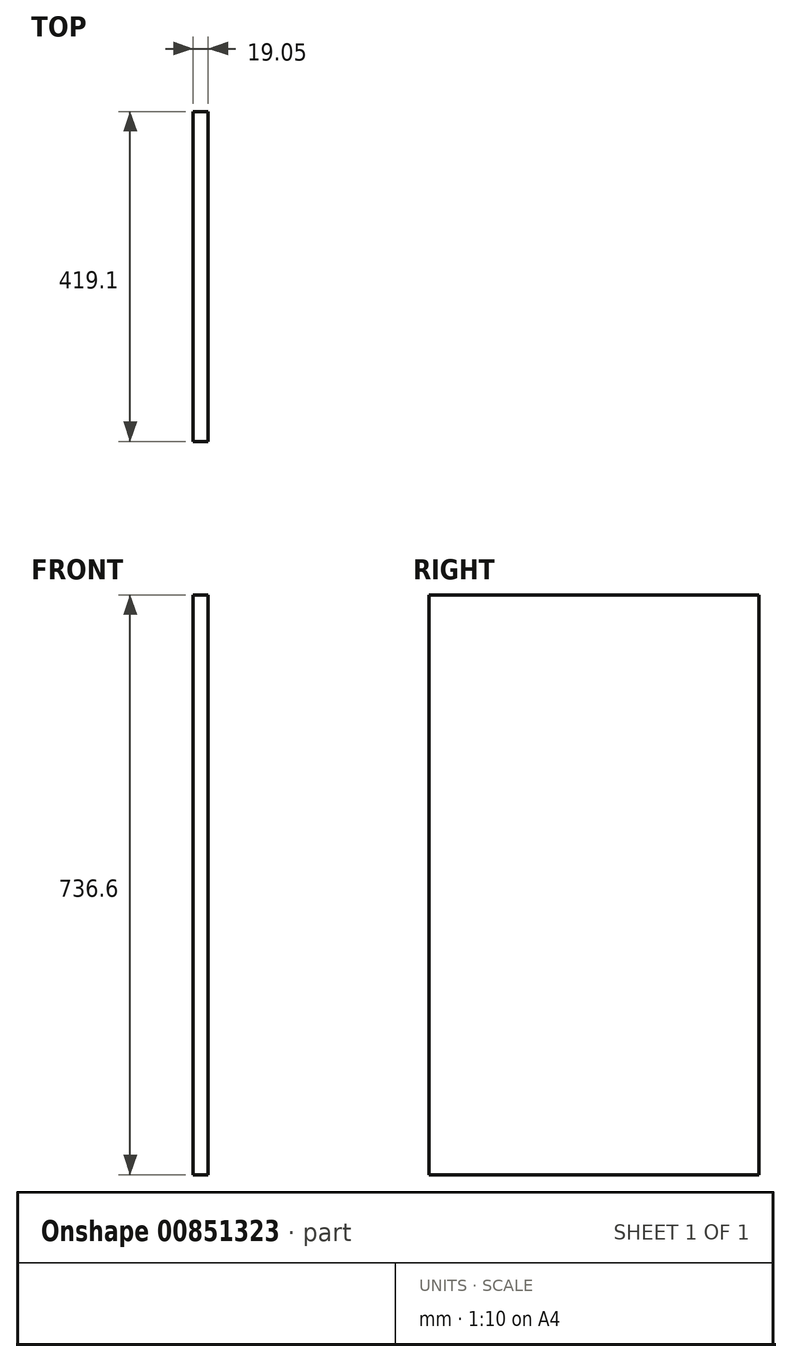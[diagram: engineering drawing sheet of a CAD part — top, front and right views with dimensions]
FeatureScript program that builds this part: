
annotation { "Feature Type Name" : "Feature", "Feature Type Description" : "" }
export const myFeature = defineFeature(function(context is Context, id is Id, definition is map)
    precondition{}
    {
        {
            var Q0;
            Q0=qCreatedBy(makeId("Right.planeOp"),FACE);
            var sketch = newSketch(context, id + "F0", { "sketchPlane" : qUnion([Q0])});
            skLineSegment(sketch, "E0", {"start": v(-419.1, 185.27) * mm, "end": v(-419.1, -551.33) * mm});
            skLineSegment(sketch, "E1", {"start": v(-419.1, -551.33) * mm, "end": v(0, -551.33) * mm});
            skLineSegment(sketch, "E2", {"start": v(0, -551.33) * mm, "end": v(0, 185.27) * mm});
            skLineSegment(sketch, "E3", {"start": v(0, 185.27) * mm, "end": v(-419.1, 185.27) * mm});
            skSolve(sketch);
        }
        {
            var Q0;
            Q0 = qSketchRegion(id + "F0", true);
            extrude(context, id + "F1", {"entities" : qUnion([Q0]), "depth" : 19.05 * mm, "offsetDistance" : 25.4 * mm});
        }
    });
